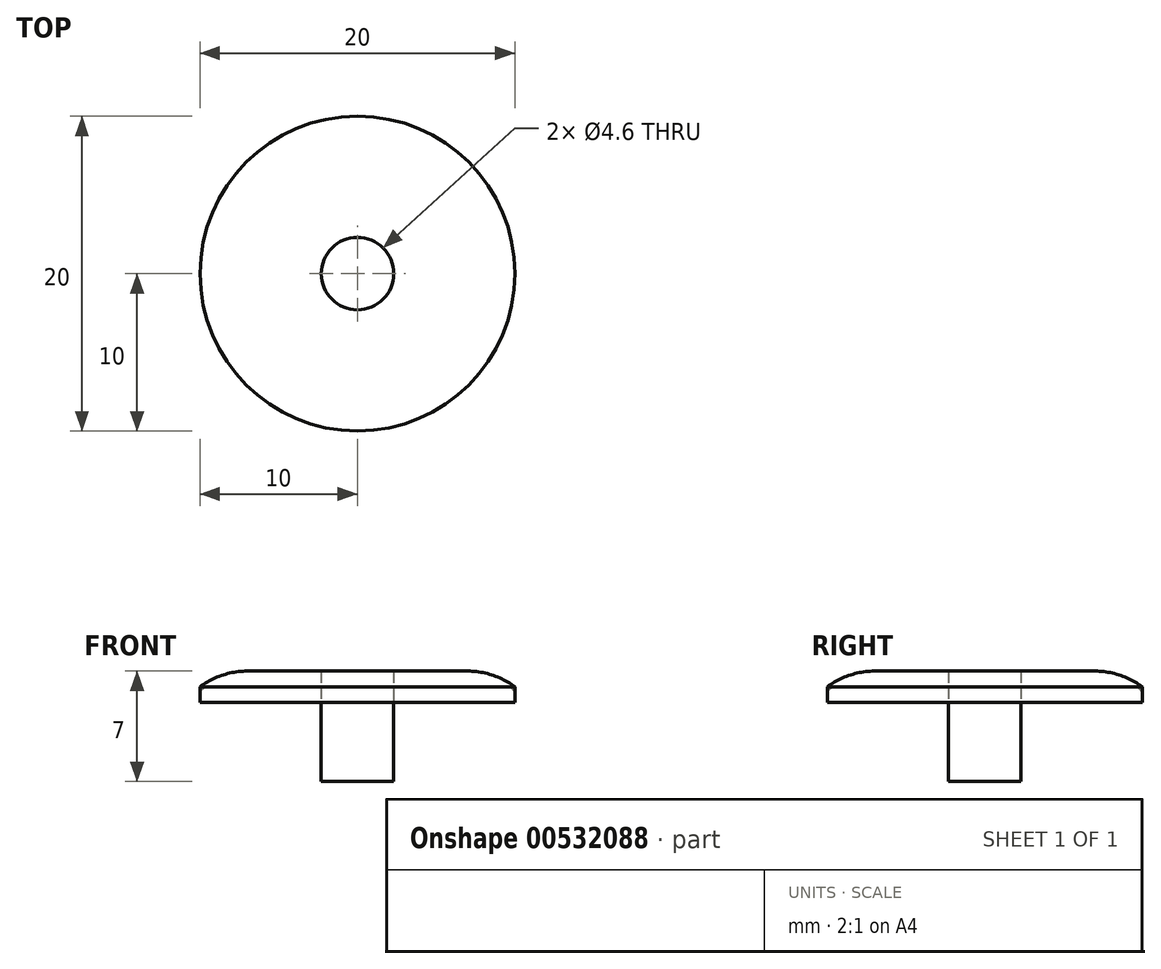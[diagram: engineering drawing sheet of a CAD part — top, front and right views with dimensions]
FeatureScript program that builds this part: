
annotation { "Feature Type Name" : "Feature", "Feature Type Description" : "" }
export const myFeature = defineFeature(function(context is Context, id is Id, definition is map)
    precondition{}
    {
        {
            var Q0;
            Q0=qCreatedBy(makeId("Top.planeOp"),FACE);
            var sketch = newSketch(context, id + "F0", { "sketchPlane" : qUnion([Q0])});
            skCircle(sketch, "E0", {"center": v(0, 0) * mm, "radius": 10 * mm});
            skCircle(sketch, "E1", {"center": v(0, 0) * mm, "radius": 2.3 * mm});
            skSolve(sketch);
        }
        {
            var Q0;
            Q0 = qSketchRegion(id + "F0", true);
            extrude(context, id + "F1", {"entities" : qUnion([Q0]), "depth" : 1 * mm, "offsetDistance" : 25 * mm});
        }
        {
            var Q0;
            Q0=makeQuery(id+"F1.opExtrude","CAP_EDGE",EDGE,{"disambiguationData":[OSD([sQuery(id+"F0.wireOp",EDGE,"E0")])],"isStart":false});
            fillet(context, id + "F2", {"entities" : qUnion([Q0]), "radius" : 0.5 * mm, "tangentPropagation" : true, "allowEdgeOverflow" : false});
        }
        {
            var Q0;
            Q0=makeQuery(id+"F0.imprint","IMPRINT",FACE,{"disambiguationData":[TD([[makeQuery(id+"F0.imprint","IMPRINT",EDGE,{"derivedFrom":sQuery(id+"F0.wireOp",EDGE,"E1")}),1.0]])]});
            extrude(context, id + "F3", {"entities" : qUnion([Q0]), "operationType" : NewBodyOperationType.ADD, "oppositeDirection" : true, "depth" : 5 * mm, "offsetDistance" : 25 * mm});
        }
        {
            var Q0;
            Q0=makeQuery(id+"F3.opExtrude","CAP_FACE",FACE,{"disambiguationData":[OSD([sQuery(id+"F0.wireOp",EDGE,"E1")])],"isStart":true});
            extrude(context, id + "F4", {"entities" : qUnion([Q0]), "depth" : 1 * mm, "offsetDistance" : 25 * mm});
        }
        {
            var Q0;
            Q0=makeQuery(id+"F1.opExtrude","CAP_FACE",FACE,{"disambiguationData":[OSD([sQuery(id+"F0.wireOp",EDGE,"E0"),sQuery(id+"F0.wireOp",EDGE,"E1")])],"isStart":true});
            extrude(context, id + "F5", {"entities" : qUnion([Q0]), "oppositeDirection" : true, "depth" : 2 * mm, "offsetDistance" : 25 * mm});
        }
        {
            var Q0;
            Q0=makeQuery(id+"F4.opExtrude","CAP_FACE",FACE,{"disambiguationData":[OSD([sQuery(id+"F0.wireOp",EDGE,"E1")])],"isStart":false});
            extrude(context, id + "F6", {"entities" : qUnion([Q0]), "depth" : 1 * mm, "offsetDistance" : 25 * mm});
        }
        {
            var Q0;
            Q0=makeQuery(id+"F5.opExtrude","CAP_EDGE",EDGE,{"disambiguationData":[OSD([sQuery(id+"F0.wireOp",EDGE,"E0")])],"isStart":false});
            chamfer(context, id + "F7", {"entities" : qUnion([Q0]), "width" : 1 * mm, "tangentPropagation" : true});
        }
        {
            var Q0;
            {var subQ0=sQuery(id+"F0.wireOp",EDGE,"E0");Q0=makeQuery(id+"F7.opChamfer","BLEND_EDGE",EDGE,{"blendedFrom":[makeQuery(id+"F5.opExtrude","CAP_EDGE",EDGE,{"disambiguationData":[OSD([subQ0])],"isStart":false}),makeQuery(id+"F5.opExtrude","CAP_FACE",FACE,{"disambiguationData":[OSD([subQ0,sQuery(id+"F0.wireOp",EDGE,"E1")])],"isStart":false})],"blendedInto":[makeQuery(id+"F5.opExtrude","CAP_FACE",FACE,{"disambiguationData":[OSD([subQ0,sQuery(id+"F0.wireOp",EDGE,"E1")])],"isStart":false})]});}
            fillet(context, id + "F8", {"entities" : qUnion([Q0]), "radius" : 5 * mm, "tangentPropagation" : true, "allowEdgeOverflow" : false});
        }
    });
